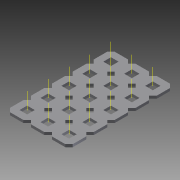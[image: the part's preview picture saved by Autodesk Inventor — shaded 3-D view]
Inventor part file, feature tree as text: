
AUTODESK INVENTOR PART (.ipt)
format: ipt  version: 2015 SP1 (Build 190203100, 203)  size: 1,132,544 bytes
history: native  units: in
note: dims shown in document units (in); Inventor stores cm internally (conversion verified against a paired STEP export)
features: other x24, extrude x2, pattern_linear x1, imported_body x1
ambient origin geometry x8: Origin, YZ Plane, XZ Plane, XY Plane, X Axis, Y Axis, Z Axis, Center Point
bodies: Body1 (feature_tree)
feature tree (28):
  other  "Diamond-Pattern"
  other  "Plate"
  extrude  "length cut"  TaperAngle=0.0deg  [1 undecoded]
  extrude  "width cut"  TaperAngle=0.0deg  [1 undecoded]
  other  "constraint axis"
  pattern_linear  "constraint axes"  Spacing1=0.5in  [1 undecoded]
  other  "front plane"
  other  "right plane"
  imported_body  "Base1"
  other  "length profile"
  other  "width profile"
  other  "Work Point1"
  other  "Work Axis36"
  other  "Work Axis37"
  other  "Work Axis38"
  other  "Work Axis40"
  other  "Work Axis41"
  other  "Work Axis42"
  other  "Work Axis43"
  other  "Work Axis44"
  other  "Work Axis45"
  other  "Work Axis46"
  other  "Work Axis47"
  other  "back plane"
  other  "left plane"
  other  "Work Axis170"
  other  "Work Axis171"
  other  "Work Axis172"
note: 3 required parameter values undecoded (feature->parameter linkage not recoverable at this tier; creation-order binding heuristic only, values carry confidence <= 0.55)
